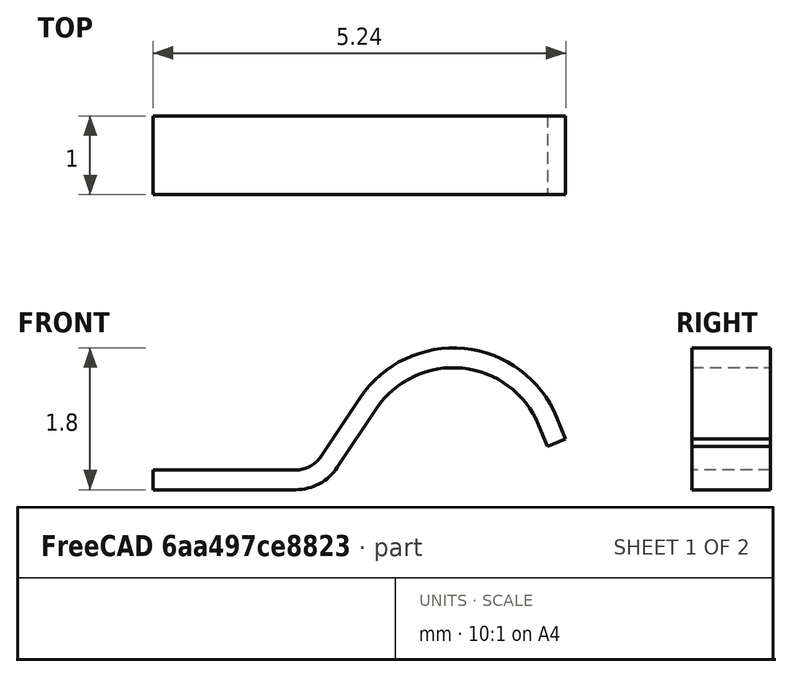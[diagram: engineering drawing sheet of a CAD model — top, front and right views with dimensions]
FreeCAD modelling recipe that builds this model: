
FCSTD DOCUMENT  (FreeCAD 0.18.4R)
Label: Amphenol_C707_10M006_052_2-spring_contact
License: All rights reserved
LicenseURL: http://en.wikipedia.org/wiki/All_rights_reserved
objects: Sketcher::SketchObject×1, PartDesign::Pad×1, PartDesign::Body×1
note: 4 computed .brp shape members not serialized (recipe doc carries the construction recipe); baked Part::Feature solids carry a one-line shape summary decoded from their .brp

FEATURE [Sketcher::SketchObject] Sketch
  MapMode = 5
  Placement = pos=(0,0,0) rot=(1,0,0;1.5708rad)
  Support = -> [XZ_Plane]
  sketch-geometry (15):
    g0: LineSegment StartX=2.33674 StartY=1.28281 StartZ=0 EndX=2.8356 EndY=2.02924 EndZ=0
    g1: LineSegment StartX=4.89307 StartY=1.82578 StartZ=0 EndX=5.00769 EndY=1.54854 EndZ=0
    g2: LineSegment StartX=0 StartY=1 StartZ=0 EndX=0 EndY=1.25 EndZ=0
    g3: ArcOfCircle CenterX=1.80757 CenterY=1.63647 CenterZ=0 NormalX=0 NormalY=0 NormalZ=1 AngleXU=0 Radius=0.636473 StartAngle=4.71239 EndAngle=5.69403
    g4: ArcOfCircle CenterX=3.81 CenterY=1.37802 CenterZ=0 NormalX=0 NormalY=0 NormalZ=1 AngleXU=0 Radius=1.17198 StartAngle=0.392021 EndAngle=2.55244
    g5: LineSegment StartX=5.00769 StartY=1.54854 StartZ=0 EndX=5.23873 EndY=1.64406 EndZ=0
    g6: LineSegment StartX=5.23873 StartY=1.64406 StartZ=0 EndX=5.12411 EndY=1.9213 EndZ=0
    g7: LineSegment StartX=0 StartY=1.25 StartZ=0 EndX=1.80757 EndY=1.25 EndZ=0
    g8: LineSegment StartX=2.12889 StartY=1.42173 StartZ=0 EndX=2.62775 EndY=2.16816 EndZ=0
    g9: ArcOfCircle CenterX=3.81 CenterY=1.37802 CenterZ=0 NormalX=0 NormalY=0 NormalZ=1 AngleXU=0 Radius=1.42198 StartAngle=0.392021 EndAngle=2.55244
    g10: ArcOfCircle CenterX=1.80757 CenterY=1.63647 CenterZ=0 NormalX=0 NormalY=0 NormalZ=1 AngleXU=0 Radius=0.386473 StartAngle=4.71239 EndAngle=5.69403
    g11: LineSegment [constr] StartX=0 StartY=2 StartZ=0 EndX=5.94744 EndY=2 EndZ=0
    g12: GeomPoint X=3.81 Y=2.8 Z=0
    g13: GeomPoint X=3.81 Y=2.55 Z=0
    g14: LineSegment StartX=0 StartY=1 StartZ=0 EndX=1.80757 EndY=1 EndZ=0
  constraints (36):
    c: Tangent(g0,g3) = -1.5708
    c: Tangent(g0,g4) = 1.5708
    c: Tangent(g1,g4) = 1.5708
    c: Coincident(g1,g5)
    c: Coincident(g5,g6)
    c: Coincident(g2,g7)
    c: Horizontal(g7)
    c: Tangent(g6,g9) = -1.5708
    c: Tangent(g8,g9) = 1.5708
    c: Perpendicular(g5,g1)
    c: Perpendicular(g6,g5)
    c: Tangent(g7,g10) = -1.5708
    c: Tangent(g8,g10) = -1.5708
    c: Parallel(g8,g0)
    c: Distance(g5) = 0.25
    c: Equal(g2,g5)
    c: PointOnObject(g11,g-2)
    c: Horizontal(g11)
    c: PointOnObject(g12,g9)
    c: Vertical(g12,g9)
    c: DistanceY(g11,g12) = 0.8
    c: PointOnObject(g13,g4)
    c: Vertical(g13,g4)
    c: DistanceY(g13,g12) = 0.25
    c: Vertical(g12,g13)
    c: DistanceX(g-1,g12) = 3.81
    c: DistanceY(g-1,g11) = 2
    c: DistanceY(g-1,g2) = 1
    c: Coincident(g14,g2)
    c: Coincident(g14,g3)
    c: Horizontal(g14)
    c: Distance(g6) = 0.3
    c: Distance(g7,g3) = 0.25
    c: Distance(g8,g0) = 0.25
    c: Vertical(g2)
    c: PointOnObject(g2,g-2)
FEATURE [PartDesign::Pad] Pad  label="SpringContact_Pad"
  Length = 1
  Length2 = 100
  Midplane = true
  Placement = pos=(0,0,0) rot=(1,0,0;1.5708rad)
  Profile = -> Sketch
  Type = 0
FEATURE [PartDesign::Body] Body  label="SpringContact"
  Group = -> [Sketch,Pad]
  Origin = -> Origin
  Tip = -> Pad
